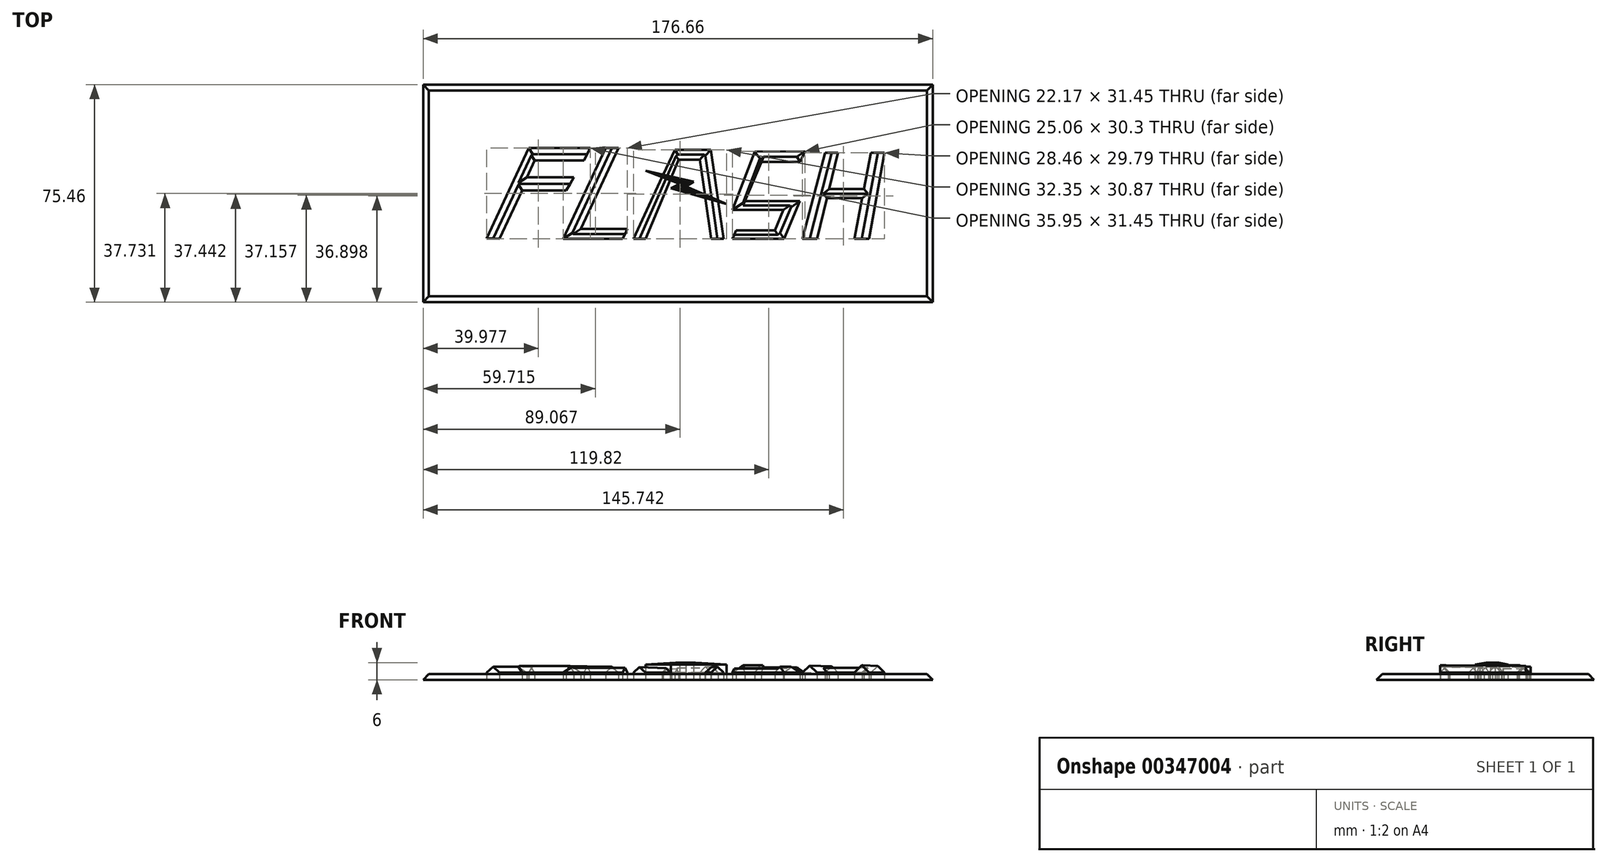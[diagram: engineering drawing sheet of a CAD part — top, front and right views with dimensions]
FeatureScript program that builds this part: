
annotation { "Feature Type Name" : "Feature", "Feature Type Description" : "" }
export const myFeature = defineFeature(function(context is Context, id is Id, definition is map)
    precondition{}
    {
        {
            var Q0;
            Q0=qCreatedBy(makeId("Top.planeOp"),FACE);
            var sketch = newSketch(context, id + "F0", { "sketchPlane" : qUnion([Q0])});
            skLineSegment(sketch, "E0", {"start": v(-57.66, -5.33) * mm, "end": v(-43.01, 25.96) * mm});
            skLineSegment(sketch, "E1", {"start": v(-43.01, 25.96) * mm, "end": v(-21.71, 25.96) * mm});
            skLineSegment(sketch, "E2", {"start": v(-21.71, 25.96) * mm, "end": v(-23.87, 21.63) * mm});
            skLineSegment(sketch, "E3", {"start": v(-23.87, 21.63) * mm, "end": v(-41.01, 21.63) * mm});
            skLineSegment(sketch, "E4", {"start": v(-41.01, 21.63) * mm, "end": v(-43.68, 15.8) * mm});
            skLineSegment(sketch, "E5", {"start": v(-43.68, 15.8) * mm, "end": v(-27.37, 15.8) * mm});
            skLineSegment(sketch, "E6", {"start": v(-27.37, 15.8) * mm, "end": v(-30.03, 11.31) * mm});
            skLineSegment(sketch, "E7", {"start": v(-30.03, 11.31) * mm, "end": v(-45.34, 11.31) * mm});
            skLineSegment(sketch, "E8", {"start": v(-45.34, 11.31) * mm, "end": v(-53.16, -5.5) * mm});
            skLineSegment(sketch, "E9", {"start": v(-53.16, -5.5) * mm, "end": v(-57.66, -5.33) * mm});
            skLineSegment(sketch, "E10", {"start": v(-16.4, 25.96) * mm, "end": v(-31.03, -5.5) * mm});
            skLineSegment(sketch, "E11", {"start": v(-31.03, -5.5) * mm, "end": v(-10.45, -5.5) * mm});
            skLineSegment(sketch, "E12", {"start": v(-10.45, -5.5) * mm, "end": v(-8.86, -2.07) * mm});
            skLineSegment(sketch, "E13", {"start": v(-8.86, -2.07) * mm, "end": v(-25, -2.07) * mm});
            skLineSegment(sketch, "E14", {"start": v(-25, -2.07) * mm, "end": v(-11.96, 25.96) * mm});
            skLineSegment(sketch, "E15", {"start": v(-11.96, 25.96) * mm, "end": v(-16.4, 25.96) * mm});
            skLineSegment(sketch, "E16", {"start": v(-6.77, -5.5) * mm, "end": v(7.6, 25.38) * mm});
            skLineSegment(sketch, "E17", {"start": v(7.6, 25.38) * mm, "end": v(20.04, 25.38) * mm});
            skLineSegment(sketch, "E18", {"start": v(20.04, 25.38) * mm, "end": v(24.51, -5.5) * mm});
            skLineSegment(sketch, "E19", {"start": v(24.51, -5.5) * mm, "end": v(20.27, -5.5) * mm});
            skLineSegment(sketch, "E20", {"start": v(20.27, -5.5) * mm, "end": v(16.3, 21.95) * mm});
            skLineSegment(sketch, "E21", {"start": v(16.3, 21.95) * mm, "end": v(8.95, 21.95) * mm});
            skLineSegment(sketch, "E22", {"start": v(8.95, 21.95) * mm, "end": v(-2.58, -5.5) * mm});
            skLineSegment(sketch, "E23", {"start": v(-2.58, -5.5) * mm, "end": v(-6.77, -5.5) * mm});
            skLineSegment(sketch, "E24", {"start": v(11.43, 12.66) * mm, "end": v(14.1, 14.3) * mm});
            skLineSegment(sketch, "E25", {"start": v(14.1, 14.3) * mm, "end": v(-2.52, 18.1) * mm});
            skLineSegment(sketch, "E26", {"start": v(-2.52, 18.1) * mm, "end": v(9.35, 13.6) * mm});
            skLineSegment(sketch, "E27", {"start": v(9.35, 13.6) * mm, "end": v(6.28, 12.02) * mm});
            skLineSegment(sketch, "E28", {"start": v(6.28, 12.02) * mm, "end": v(25.58, 6.58) * mm});
            skLineSegment(sketch, "E29", {"start": v(25.58, 6.58) * mm, "end": v(11.43, 12.66) * mm});
            skLineSegment(sketch, "E30", {"start": v(27.63, -5.5) * mm, "end": v(45.48, -5.5) * mm});
            skLineSegment(sketch, "E31", {"start": v(45.48, -5.5) * mm, "end": v(50.95, 7.53) * mm});
            skLineSegment(sketch, "E32", {"start": v(50.95, 7.53) * mm, "end": v(31.92, 7.53) * mm});
            skLineSegment(sketch, "E33", {"start": v(31.92, 7.53) * mm, "end": v(37.67, 21.22) * mm});
            skLineSegment(sketch, "E34", {"start": v(37.67, 21.22) * mm, "end": v(51.02, 21.22) * mm});
            skLineSegment(sketch, "E35", {"start": v(51.02, 21.22) * mm, "end": v(52.69, 24.8) * mm});
            skLineSegment(sketch, "E36", {"start": v(27.63, -5.5) * mm, "end": v(28.86, -2.63) * mm});
            skLineSegment(sketch, "E37", {"start": v(28.86, -2.63) * mm, "end": v(42.36, -2.63) * mm});
            skLineSegment(sketch, "E38", {"start": v(42.36, -2.63) * mm, "end": v(45.23, 4.5) * mm});
            skLineSegment(sketch, "E39", {"start": v(45.23, 4.5) * mm, "end": v(27.63, 4.5) * mm});
            skLineSegment(sketch, "E40", {"start": v(27.63, 4.5) * mm, "end": v(35.36, 24.8) * mm});
            skLineSegment(sketch, "E41", {"start": v(35.36, 24.8) * mm, "end": v(52.69, 24.8) * mm});
            skLineSegment(sketch, "E42", {"start": v(59.74, 24.3) * mm, "end": v(51.85, -5.5) * mm});
            skPoint(sketch, "E42.endSnap0", {"position": v(51.85, 23.01) * mm});
            skLineSegment(sketch, "E43", {"start": v(51.85, -5.5) * mm, "end": v(56.96, -5.5) * mm});
            skLineSegment(sketch, "E44", {"start": v(56.96, -5.5) * mm, "end": v(60.38, 8.57) * mm});
            skLineSegment(sketch, "E45", {"start": v(64.22, 24.3) * mm, "end": v(59.74, 24.3) * mm});
            skLineSegment(sketch, "E46", {"start": v(69.89, -5.5) * mm, "end": v(75, -5.5) * mm});
            skLineSegment(sketch, "E47", {"start": v(75, -5.5) * mm, "end": v(80.31, 24.3) * mm});
            skLineSegment(sketch, "E48", {"start": v(80.31, 24.3) * mm, "end": v(75.62, 24.3) * mm});
            skLineSegment(sketch, "E49", {"start": v(75.62, 24.3) * mm, "end": v(73.2, 11.76) * mm});
            skLineSegment(sketch, "E50", {"start": v(61.16, 11.76) * mm, "end": v(73.2, 11.76) * mm});
            skLineSegment(sketch, "E51", {"start": v(72.6, 8.57) * mm, "end": v(60.38, 8.57) * mm});
            skLineSegment(sketch, "E52.trimOffspring", {"start": v(61.16, 11.76) * mm, "end": v(64.22, 24.3) * mm});
            skLineSegment(sketch, "E53.trimOffspring", {"start": v(72.6, 8.57) * mm, "end": v(69.89, -5.5) * mm});
            skLineSegment(sketch, "E54.bottom", {"start": v(-77.66, 45.96) * mm, "end": v(95, 45.96) * mm});
            skLineSegment(sketch, "E54.top", {"start": v(-77.66, -25.5) * mm, "end": v(95, -25.5) * mm});
            skLineSegment(sketch, "E54.left", {"start": v(-77.66, 45.96) * mm, "end": v(-77.66, -25.5) * mm});
            skLineSegment(sketch, "E54.right", {"start": v(95, 45.96) * mm, "end": v(95, -25.5) * mm});
            skLineSegment(sketch, "E55.bottom", {"start": v(-79.66, 47.96) * mm, "end": v(97, 47.96) * mm});
            skLineSegment(sketch, "E55.top", {"start": v(-79.66, -27.5) * mm, "end": v(97, -27.5) * mm});
            skLineSegment(sketch, "E55.left", {"start": v(-79.66, 47.96) * mm, "end": v(-79.66, -27.5) * mm});
            skLineSegment(sketch, "E55.right", {"start": v(97, 47.96) * mm, "end": v(97, -27.5) * mm});
            skSolve(sketch);
        }
        {
            var Q0;
            Q0=makeQuery(id+"F0.imprint","IMPRINT",FACE,{"disambiguationData":[TD([[makeQuery(id+"F0.imprint","IMPRINT",EDGE,{"derivedFrom":sQuery(id+"F0.wireOp",EDGE,"E0")}),-1.0]])]});
            extrude(context, id + "F1", {"entities" : qUnion([Q0]), "depth" : 5 * mm});
        }
        {
            var Q0;
            Q0=makeQuery(id+"F1.opExtrude","CAP_EDGE",EDGE,{"disambiguationData":[OSD([sQuery(id+"F0.wireOp",EDGE,"E8")])],"isStart":false});
            chamfer(context, id + "F2", {"entities" : qUnion([Q0]), "width" : 2.5 * mm, "tangentPropagation" : true});
        }
        {
            var Q0;
            Q0=makeQuery(id+"F1.opExtrude","CAP_EDGE",EDGE,{"disambiguationData":[OSD([sQuery(id+"F0.wireOp",EDGE,"E7")])],"isStart":false});
            chamfer(context, id + "F3", {"entities" : qUnion([Q0]), "width" : 2.5 * mm, "tangentPropagation" : true});
        }
        {
            var Q0;
            Q0=makeQuery(id+"F1.opExtrude","CAP_EDGE",EDGE,{"disambiguationData":[OSD([sQuery(id+"F0.wireOp",EDGE,"E4")])],"isStart":false});
            chamfer(context, id + "F4", {"entities" : qUnion([Q0]), "width" : 2.5 * mm, "tangentPropagation" : true});
        }
        {
            var Q0;
            Q0=makeQuery(id+"F1.opExtrude","CAP_EDGE",EDGE,{"disambiguationData":[OSD([sQuery(id+"F0.wireOp",EDGE,"E3")])],"isStart":false});
            chamfer(context, id + "F5", {"entities" : qUnion([Q0]), "width" : 2.5 * mm, "tangentPropagation" : true});
        }
        {
            var Q0;
            Q0=makeQuery(id+"F1.opExtrude","CAP_EDGE",EDGE,{"disambiguationData":[OSD([sQuery(id+"F0.wireOp",EDGE,"E1")])],"isStart":false});
            chamfer(context, id + "F6", {"entities" : qUnion([Q0]), "width" : 2.5 * mm, "tangentPropagation" : true});
        }
        {
            var Q0;
            Q0=makeQuery(id+"F1.opExtrude","CAP_EDGE",EDGE,{"disambiguationData":[OSD([sQuery(id+"F0.wireOp",EDGE,"E0")])],"isStart":false});
            chamfer(context, id + "F7", {"entities" : qUnion([Q0]), "width" : 2.5 * mm, "tangentPropagation" : true});
        }
        {
            var Q0;
            Q0=makeQuery(id+"F0.imprint","IMPRINT",FACE,{"disambiguationData":[TD([[makeQuery(id+"F0.imprint","IMPRINT",EDGE,{"derivedFrom":sQuery(id+"F0.wireOp",EDGE,"E10")}),1.0]])]});
            extrude(context, id + "F8", {"entities" : qUnion([Q0]), "depth" : 5 * mm});
        }
        {
            var Q0;
            Q0=makeQuery(id+"F8.opExtrude","CAP_EDGE",EDGE,{"disambiguationData":[OSD([sQuery(id+"F0.wireOp",EDGE,"E11")])],"isStart":false});
            chamfer(context, id + "F9", {"entities" : qUnion([Q0]), "width" : 2.5 * mm, "tangentPropagation" : true});
        }
        {
            var Q0;
            Q0=makeQuery(id+"F8.opExtrude","CAP_EDGE",EDGE,{"disambiguationData":[OSD([sQuery(id+"F0.wireOp",EDGE,"E10")])],"isStart":false});
            chamfer(context, id + "F10", {"entities" : qUnion([Q0]), "width" : 2.5 * mm, "tangentPropagation" : true});
        }
        {
            var Q0;
            Q0=makeQuery(id+"F8.opExtrude","CAP_EDGE",EDGE,{"disambiguationData":[OSD([sQuery(id+"F0.wireOp",EDGE,"E13")])],"isStart":false});
            chamfer(context, id + "F11", {"entities" : qUnion([Q0]), "width" : 2.5 * mm, "tangentPropagation" : true});
        }
        {
            var Q0;
            Q0=makeQuery(id+"F8.opExtrude","CAP_EDGE",EDGE,{"disambiguationData":[OSD([sQuery(id+"F0.wireOp",EDGE,"E14")])],"isStart":false});
            chamfer(context, id + "F12", {"entities" : qUnion([Q0]), "width" : 2.5 * mm, "tangentPropagation" : true});
        }
        {
            var Q0;
            {var subQ5=sQuery(id+"F0.wireOp",EDGE,"E17");Q0=makeQuery(id+"F0.imprint","IMPRINT",FACE,{"disambiguationData":[TD([[makeQuery(id+"F0.imprint","IMPRINT",EDGE,{"derivedFrom":subQ5}),-1.0]])]});}
            var Q1;
            {var subQ0=sQuery(id+"F0.wireOp",EDGE,"E19");Q1=makeQuery(id+"F0.imprint","IMPRINT",FACE,{"disambiguationData":[TD([[makeQuery(id+"F0.imprint","IMPRINT",EDGE,{"derivedFrom":subQ0}),-1.0]])]});}
            var Q2;
            {var subQ0=sQuery(id+"F0.wireOp",EDGE,"E23");Q2=makeQuery(id+"F0.imprint","IMPRINT",FACE,{"disambiguationData":[TD([[makeQuery(id+"F0.imprint","IMPRINT",EDGE,{"derivedFrom":subQ0}),-1.0]])]});}
            extrude(context, id + "F13", {"entities" : qUnion([Q0, Q1, Q2]), "depth" : 5 * mm});
        }
        {
            var Q0;
            {var subQ1=sQuery(id+"F0.wireOp",EDGE,"E24");Q0=makeQuery(id+"F0.imprint","IMPRINT",FACE,{"disambiguationData":[TD([[makeQuery(id+"F0.imprint","IMPRINT",EDGE,{"derivedFrom":subQ1}),1.0]])]});}
            var Q1;
            {var subQ0=sQuery(id+"F0.wireOp",EDGE,"E26");var subQ1=sQuery(id+"F0.wireOp",EDGE,"E16");var subQ2=makeQuery(id+"F0.imprint","INTERSECT",VERTEX,{"derivedFrom":[subQ1,subQ0]});Q1=makeQuery(id+"F0.imprint","IMPRINT",FACE,{"disambiguationData":[TD([[makeQuery(id+"F0.imprint","IMPRINT",EDGE,{"disambiguationData":[TD([[subQ2,-1.0]])],"derivedFrom":subQ1}),1.0]])]});}
            var Q2;
            {var subQ0=sQuery(id+"F0.wireOp",EDGE,"E26");var subQ1=sQuery(id+"F0.wireOp",EDGE,"E16");var subQ2=makeQuery(id+"F0.imprint","INTERSECT",VERTEX,{"derivedFrom":[subQ1,subQ0]});Q2=makeQuery(id+"F0.imprint","IMPRINT",FACE,{"disambiguationData":[TD([[makeQuery(id+"F0.imprint","IMPRINT",EDGE,{"disambiguationData":[TD([[subQ2,-1.0]])],"derivedFrom":subQ1}),-1.0]])]});}
            var Q3;
            {var subQ0=sQuery(id+"F0.wireOp",EDGE,"E29");var subQ1=sQuery(id+"F0.wireOp",EDGE,"E18");var subQ2=makeQuery(id+"F0.imprint","INTERSECT",VERTEX,{"derivedFrom":[subQ1,subQ0]});Q3=makeQuery(id+"F0.imprint","IMPRINT",FACE,{"disambiguationData":[TD([[makeQuery(id+"F0.imprint","IMPRINT",EDGE,{"disambiguationData":[TD([[subQ2,-1.0]])],"derivedFrom":subQ1}),-1.0]])]});}
            var Q4;
            {var subQ0=sQuery(id+"F0.wireOp",EDGE,"E29");var subQ1=sQuery(id+"F0.wireOp",EDGE,"E18");var subQ2=makeQuery(id+"F0.imprint","INTERSECT",VERTEX,{"derivedFrom":[subQ1,subQ0]});Q4=makeQuery(id+"F0.imprint","IMPRINT",FACE,{"disambiguationData":[TD([[makeQuery(id+"F0.imprint","IMPRINT",EDGE,{"disambiguationData":[TD([[subQ2,-1.0]])],"derivedFrom":subQ1}),1.0]])]});}
            extrude(context, id + "F14", {"entities" : qUnion([Q0, Q1, Q2, Q3, Q4]), "depth" : 6 * mm});
        }
        {
            var Q0;
            {var subQ0=sQuery(id+"F0.wireOp",EDGE,"E22");Q0=makeQuery(id+"F13.opExtrude","CAP_EDGE",EDGE,{"disambiguationData":[OSD([subQ0]),TDD([makeQuery(id+"F0.imprint","IMPRINT",EDGE,{"disambiguationData":[TD([[makeQuery(id+"F0.imprint","INTERSECT",VERTEX,{"derivedFrom":[subQ0,sQuery(id+"F0.wireOp",EDGE,"E23")]}),1.0]])],"derivedFrom":subQ0})])],"isStart":false});}
            chamfer(context, id + "F15", {"entities" : qUnion([Q0]), "width" : 2.5 * mm, "tangentPropagation" : true});
        }
        {
            var Q0;
            {var subQ0=sQuery(id+"F0.wireOp",EDGE,"E20");Q0=makeQuery(id+"F13.opExtrude","CAP_EDGE",EDGE,{"disambiguationData":[OSD([subQ0]),TDD([makeQuery(id+"F0.imprint","IMPRINT",EDGE,{"disambiguationData":[TD([[makeQuery(id+"F0.imprint","INTERSECT",VERTEX,{"derivedFrom":[sQuery(id+"F0.wireOp",EDGE,"E19"),subQ0]}),-1.0]])],"derivedFrom":subQ0})])],"isStart":false});}
            chamfer(context, id + "F16", {"entities" : qUnion([Q0]), "width" : 2.5 * mm, "tangentPropagation" : true});
        }
        {
            var Q0;
            {var subQ0=sQuery(id+"F0.wireOp",EDGE,"E16");Q0=makeQuery(id+"F13.opExtrude","CAP_EDGE",EDGE,{"disambiguationData":[OSD([subQ0]),TDD([makeQuery(id+"F0.imprint","IMPRINT",EDGE,{"disambiguationData":[TD([[makeQuery(id+"F0.imprint","INTERSECT",VERTEX,{"derivedFrom":[subQ0,sQuery(id+"F0.wireOp",EDGE,"E23")]}),-1.0]])],"derivedFrom":subQ0})])],"isStart":false});}
            var Q1;
            {var subQ0=sQuery(id+"F0.wireOp",EDGE,"E18");Q1=makeQuery(id+"F13.opExtrude","CAP_EDGE",EDGE,{"disambiguationData":[OSD([subQ0]),TDD([makeQuery(id+"F0.imprint","IMPRINT",EDGE,{"disambiguationData":[TD([[makeQuery(id+"F0.imprint","INTERSECT",VERTEX,{"derivedFrom":[subQ0,sQuery(id+"F0.wireOp",EDGE,"E19")]}),1.0]])],"derivedFrom":subQ0})])],"isStart":false});}
            var Q2;
            {var subQ0=sQuery(id+"F0.wireOp",EDGE,"E20");Q2=makeQuery(id+"F13.opExtrude","CAP_EDGE",EDGE,{"disambiguationData":[OSD([subQ0]),TDD([makeQuery(id+"F0.imprint","IMPRINT",EDGE,{"disambiguationData":[TD([[makeQuery(id+"F0.imprint","INTERSECT",VERTEX,{"derivedFrom":[subQ0,sQuery(id+"F0.wireOp",EDGE,"E21")]}),1.0]])],"derivedFrom":subQ0})])],"isStart":false});}
            var Q3;
            Q3=makeQuery(id+"F13.opExtrude","CAP_EDGE",EDGE,{"disambiguationData":[OSD([sQuery(id+"F0.wireOp",EDGE,"E21")])],"isStart":false});
            var Q4;
            {var subQ0=sQuery(id+"F0.wireOp",EDGE,"E22");Q4=makeQuery(id+"F13.opExtrude","CAP_EDGE",EDGE,{"disambiguationData":[OSD([subQ0]),TDD([makeQuery(id+"F0.imprint","IMPRINT",EDGE,{"disambiguationData":[TD([[makeQuery(id+"F0.imprint","INTERSECT",VERTEX,{"derivedFrom":[sQuery(id+"F0.wireOp",EDGE,"E21"),subQ0]}),-1.0]])],"derivedFrom":subQ0})])],"isStart":false});}
            var Q5;
            {var subQ0=sQuery(id+"F0.wireOp",EDGE,"E16");Q5=makeQuery(id+"F13.opExtrude","CAP_EDGE",EDGE,{"disambiguationData":[OSD([subQ0]),TDD([makeQuery(id+"F0.imprint","IMPRINT",EDGE,{"disambiguationData":[TD([[makeQuery(id+"F0.imprint","INTERSECT",VERTEX,{"derivedFrom":[subQ0,sQuery(id+"F0.wireOp",EDGE,"E17")]}),1.0]])],"derivedFrom":subQ0})])],"isStart":false});}
            var Q6;
            Q6=makeQuery(id+"F13.opExtrude","CAP_EDGE",EDGE,{"disambiguationData":[OSD([sQuery(id+"F0.wireOp",EDGE,"E17")])],"isStart":false});
            var Q7;
            {var subQ0=sQuery(id+"F0.wireOp",EDGE,"E18");Q7=makeQuery(id+"F13.opExtrude","CAP_EDGE",EDGE,{"disambiguationData":[OSD([subQ0]),TDD([makeQuery(id+"F0.imprint","IMPRINT",EDGE,{"disambiguationData":[TD([[makeQuery(id+"F0.imprint","INTERSECT",VERTEX,{"derivedFrom":[sQuery(id+"F0.wireOp",EDGE,"E17"),subQ0]}),-1.0]])],"derivedFrom":subQ0})])],"isStart":false});}
            chamfer(context, id + "F17", {"entities" : qUnion([Q0, Q1, Q2, Q3, Q4, Q5, Q6, Q7]), "width" : 2.5 * mm, "tangentPropagation" : true});
        }
        {
            var Q0;
            Q0=makeQuery(id+"F14.opExtrude","CAP_EDGE",EDGE,{"disambiguationData":[OSD([sQuery(id+"F0.wireOp",EDGE,"E28")])],"isStart":false});
            var Q1;
            Q1=makeQuery(id+"F14.opExtrude","CAP_EDGE",EDGE,{"disambiguationData":[OSD([sQuery(id+"F0.wireOp",EDGE,"E27")])],"isStart":false});
            var Q2;
            Q2=makeQuery(id+"F14.opExtrude","CAP_EDGE",EDGE,{"disambiguationData":[OSD([sQuery(id+"F0.wireOp",EDGE,"E24")])],"isStart":false});
            var Q3;
            Q3=makeQuery(id+"F14.opExtrude","CAP_EDGE",EDGE,{"disambiguationData":[OSD([sQuery(id+"F0.wireOp",EDGE,"E25")])],"isStart":false});
            var Q4;
            Q4=makeQuery(id+"F14.opExtrude","CAP_EDGE",EDGE,{"disambiguationData":[OSD([sQuery(id+"F0.wireOp",EDGE,"E26")])],"isStart":false});
            var Q5;
            Q5=makeQuery(id+"F14.opExtrude","CAP_EDGE",EDGE,{"disambiguationData":[OSD([sQuery(id+"F0.wireOp",EDGE,"E29")])],"isStart":false});
            chamfer(context, id + "F18", {"entities" : qUnion([Q0, Q1, Q2, Q3, Q4, Q5]), "width" : .75 * mm, "tangentPropagation" : true});
        }
        {
            var Q0;
            Q0=makeQuery(id+"F0.imprint","IMPRINT",FACE,{"disambiguationData":[TD([[makeQuery(id+"F0.imprint","IMPRINT",EDGE,{"derivedFrom":sQuery(id+"F0.wireOp",EDGE,"E30")}),1.0]])]});
            extrude(context, id + "F19", {"entities" : qUnion([Q0]), "depth" : 5 * mm});
        }
        {
            var Q0;
            Q0=makeQuery(id+"F19.opExtrude","CAP_EDGE",EDGE,{"disambiguationData":[OSD([sQuery(id+"F0.wireOp",EDGE,"E31")])],"isStart":false});
            var Q1;
            Q1=makeQuery(id+"F19.opExtrude","CAP_EDGE",EDGE,{"disambiguationData":[OSD([sQuery(id+"F0.wireOp",EDGE,"E30")])],"isStart":false});
            var Q2;
            Q2=makeQuery(id+"F19.opExtrude","CAP_EDGE",EDGE,{"disambiguationData":[OSD([sQuery(id+"F0.wireOp",EDGE,"E39")])],"isStart":false});
            var Q3;
            Q3=makeQuery(id+"F19.opExtrude","CAP_EDGE",EDGE,{"disambiguationData":[OSD([sQuery(id+"F0.wireOp",EDGE,"E40")])],"isStart":false});
            var Q4;
            Q4=makeQuery(id+"F19.opExtrude","CAP_EDGE",EDGE,{"disambiguationData":[OSD([sQuery(id+"F0.wireOp",EDGE,"E34")])],"isStart":false});
            var Q5;
            Q5=makeQuery(id+"F19.opExtrude","CAP_EDGE",EDGE,{"disambiguationData":[OSD([sQuery(id+"F0.wireOp",EDGE,"E35")])],"isStart":false});
            chamfer(context, id + "F20", {"entities" : qUnion([Q0, Q1, Q2, Q3, Q4, Q5]), "width" : 2.5 * mm, "tangentPropagation" : true});
        }
        {
            var Q0;
            Q0=makeQuery(id+"F19.opExtrude","CAP_EDGE",EDGE,{"disambiguationData":[OSD([sQuery(id+"F0.wireOp",EDGE,"E41")])],"isStart":false});
            var Q1;
            Q1=makeQuery(id+"F19.opExtrude","CAP_EDGE",EDGE,{"disambiguationData":[OSD([sQuery(id+"F0.wireOp",EDGE,"E32")])],"isStart":false});
            var Q2;
            Q2=makeQuery(id+"F19.opExtrude","CAP_EDGE",EDGE,{"disambiguationData":[OSD([sQuery(id+"F0.wireOp",EDGE,"E37")])],"isStart":false});
            chamfer(context, id + "F21", {"entities" : qUnion([Q0, Q1, Q2]), "width" : 2.5 * mm, "tangentPropagation" : true});
        }
        {
            var Q0;
            Q0=makeQuery(id+"F0.imprint","IMPRINT",FACE,{"disambiguationData":[TD([[makeQuery(id+"F0.imprint","IMPRINT",EDGE,{"derivedFrom":sQuery(id+"F0.wireOp",EDGE,"E42")}),1.0]])]});
            extrude(context, id + "F22", {"entities" : qUnion([Q0]), "depth" : 5 * mm});
        }
        {
            var Q0;
            Q0=makeQuery(id+"F22.opExtrude","CAP_EDGE",EDGE,{"disambiguationData":[OSD([sQuery(id+"F0.wireOp",EDGE,"E44")])],"isStart":false});
            var Q1;
            Q1=makeQuery(id+"F22.opExtrude","CAP_EDGE",EDGE,{"disambiguationData":[OSD([sQuery(id+"F0.wireOp",EDGE,"E42")])],"isStart":false});
            var Q2;
            Q2=makeQuery(id+"F22.opExtrude","CAP_EDGE",EDGE,{"disambiguationData":[OSD([sQuery(id+"F0.wireOp",EDGE,"E52.trimOffspring")])],"isStart":false});
            var Q3;
            Q3=makeQuery(id+"F22.opExtrude","CAP_EDGE",EDGE,{"disambiguationData":[OSD([sQuery(id+"F0.wireOp",EDGE,"E49")])],"isStart":false});
            var Q4;
            Q4=makeQuery(id+"F22.opExtrude","CAP_EDGE",EDGE,{"disambiguationData":[OSD([sQuery(id+"F0.wireOp",EDGE,"E47")])],"isStart":false});
            var Q5;
            Q5=makeQuery(id+"F22.opExtrude","CAP_EDGE",EDGE,{"disambiguationData":[OSD([sQuery(id+"F0.wireOp",EDGE,"E53.trimOffspring")])],"isStart":false});
            var Q6;
            Q6=makeQuery(id+"F22.opExtrude","CAP_EDGE",EDGE,{"disambiguationData":[OSD([sQuery(id+"F0.wireOp",EDGE,"E51")])],"isStart":false});
            var Q7;
            Q7=makeQuery(id+"F22.opExtrude","CAP_EDGE",EDGE,{"disambiguationData":[OSD([sQuery(id+"F0.wireOp",EDGE,"E50")])],"isStart":false});
            chamfer(context, id + "F23", {"entities" : qUnion([Q0, Q1, Q2, Q3, Q4, Q5, Q6, Q7]), "width" : 2.5 * mm, "tangentPropagation" : true});
        }
        {
            var Q0;
            Q0=makeQuery(id+"F0.imprint","IMPRINT",FACE,{"disambiguationData":[TD([[makeQuery(id+"F0.imprint","IMPRINT",EDGE,{"derivedFrom":sQuery(id+"F0.wireOp",EDGE,"E0")}),1.0]])]});
            extrude(context, id + "F24", {"entities" : qUnion([Q0]), "depth" : 2 * mm});
        }
        {
            var Q0;
            {var subQ1=sQuery(id+"F0.wireOp",EDGE,"E21");Q0=makeQuery(id+"F0.imprint","IMPRINT",FACE,{"disambiguationData":[TD([[makeQuery(id+"F0.imprint","IMPRINT",EDGE,{"derivedFrom":subQ1}),1.0]])]});}
            extrude(context, id + "F25", {"entities" : qUnion([Q0]), "depth" : 2 * mm});
        }
        {
            var Q0;
            Q0=makeQuery(id+"F0.imprint","IMPRINT",FACE,{"disambiguationData":[TD([[makeQuery(id+"F0.imprint","IMPRINT",EDGE,{"derivedFrom":sQuery(id+"F0.wireOp",EDGE,"E54.bottom")}),1.0]])]});
            extrude(context, id + "F26", {"entities" : qUnion([Q0]), "operationType" : NewBodyOperationType.ADD, "depth" : 3 * mm});
        }
        {
            var Q0;
            Q0=makeQuery(id+"F26.opExtrude","CAP_EDGE",EDGE,{"disambiguationData":[OSD([sQuery(id+"F0.wireOp",EDGE,"E54.bottom")])],"isStart":false});
            var Q1;
            Q1=makeQuery(id+"F26.opExtrude","CAP_EDGE",EDGE,{"disambiguationData":[OSD([sQuery(id+"F0.wireOp",EDGE,"E54.left")])],"isStart":false});
            var Q2;
            Q2=makeQuery(id+"F26.opExtrude","CAP_EDGE",EDGE,{"disambiguationData":[OSD([sQuery(id+"F0.wireOp",EDGE,"E54.top")])],"isStart":false});
            var Q3;
            Q3=makeQuery(id+"F26.opExtrude","CAP_EDGE",EDGE,{"disambiguationData":[OSD([sQuery(id+"F0.wireOp",EDGE,"E54.right")])],"isStart":false});
            chamfer(context, id + "F27", {"entities" : qUnion([Q0, Q1, Q2, Q3]), "width" : 1 * mm, "tangentPropagation" : true});
        }
        {
            var Q0;
            Q0=makeQuery(id+"F1.opExtrude","CAP_EDGE",EDGE,{"disambiguationData":[OSD([sQuery(id+"F0.wireOp",EDGE,"E5")])],"isStart":false});
            chamfer(context, id + "F28", {"entities" : qUnion([Q0]), "width" : 2.5 * mm, "tangentPropagation" : true});
        }
        {
            var Q0;
            Q0=makeQuery(id+"F19.opExtrude","CAP_EDGE",EDGE,{"disambiguationData":[OSD([sQuery(id+"F0.wireOp",EDGE,"E38")])],"isStart":false});
            chamfer(context, id + "F29", {"entities" : qUnion([Q0]), "width" : 2.5 * mm, "tangentPropagation" : true});
        }
        {
            var Q0;
            Q0=makeQuery(id+"F26.opExtrude","CAP_EDGE",EDGE,{"disambiguationData":[OSD([sQuery(id+"F0.wireOp",EDGE,"E55.top")])],"isStart":false});
            var Q1;
            Q1=makeQuery(id+"F26.opExtrude","CAP_EDGE",EDGE,{"disambiguationData":[OSD([sQuery(id+"F0.wireOp",EDGE,"E55.left")])],"isStart":false});
            var Q2;
            Q2=makeQuery(id+"F26.opExtrude","CAP_EDGE",EDGE,{"disambiguationData":[OSD([sQuery(id+"F0.wireOp",EDGE,"E55.right")])],"isStart":false});
            var Q3;
            Q3=makeQuery(id+"F26.opExtrude","CAP_EDGE",EDGE,{"disambiguationData":[OSD([sQuery(id+"F0.wireOp",EDGE,"E55.bottom")])],"isStart":false});
            chamfer(context, id + "F30", {"entities" : qUnion([Q0, Q1, Q2, Q3]), "width" : 3 * mm, "tangentPropagation" : true});
        }
    });
